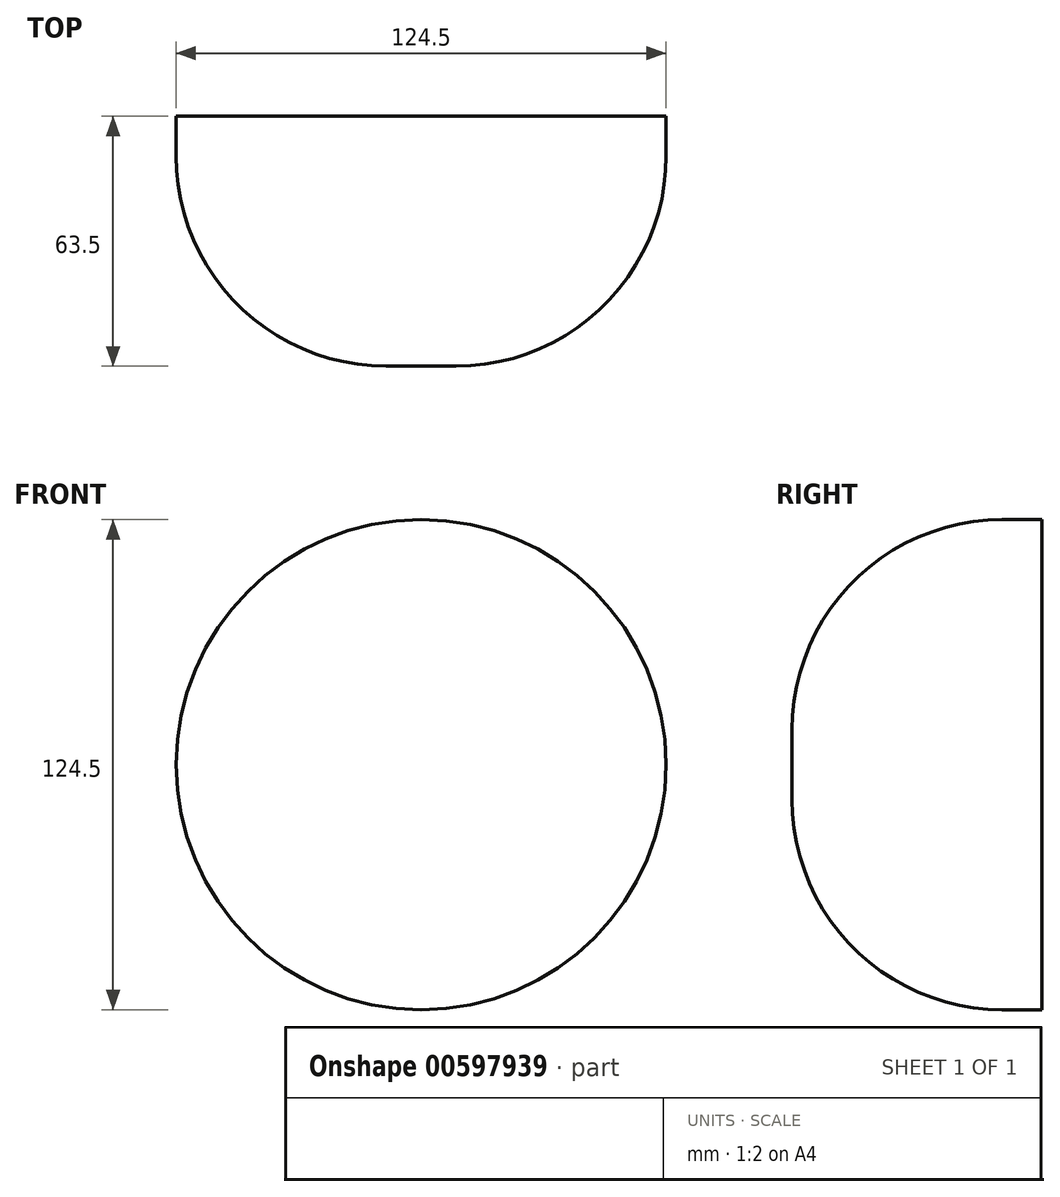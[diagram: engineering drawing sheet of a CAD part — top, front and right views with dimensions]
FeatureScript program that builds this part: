
annotation { "Feature Type Name" : "Feature", "Feature Type Description" : "" }
export const myFeature = defineFeature(function(context is Context, id is Id, definition is map)
    precondition{}
    {
        {
            var Q0;
            Q0=qCreatedBy(makeId("Front.planeOp"),FACE);
            var sketch = newSketch(context, id + "F0", { "sketchPlane" : qUnion([Q0])});
            skCircle(sketch, "E0", {"center": v(0, 0) * mm, "radius": 62.25 * mm});
            skSolve(sketch);
        }
        {
            var Q0;
            Q0 = qSketchRegion(id + "F0", true);
            extrude(context, id + "F1", {"entities" : qUnion([Q0]), "depth" : 63.5 * mm, "offsetDistance" : 25.4 * mm});
        }
        {
            var Q0;
            Q0=makeQuery(id+"F1.opExtrude","CAP_FACE",FACE,{"disambiguationData":[OSD([sQuery(id+"F0.wireOp",EDGE,"E0")])],"isStart":false});
            fillet(context, id + "F2", {"entities" : qUnion([Q0]), "radius" : 53.34 * mm, "tangentPropagation" : true, "allowEdgeOverflow" : false});
        }
    });
